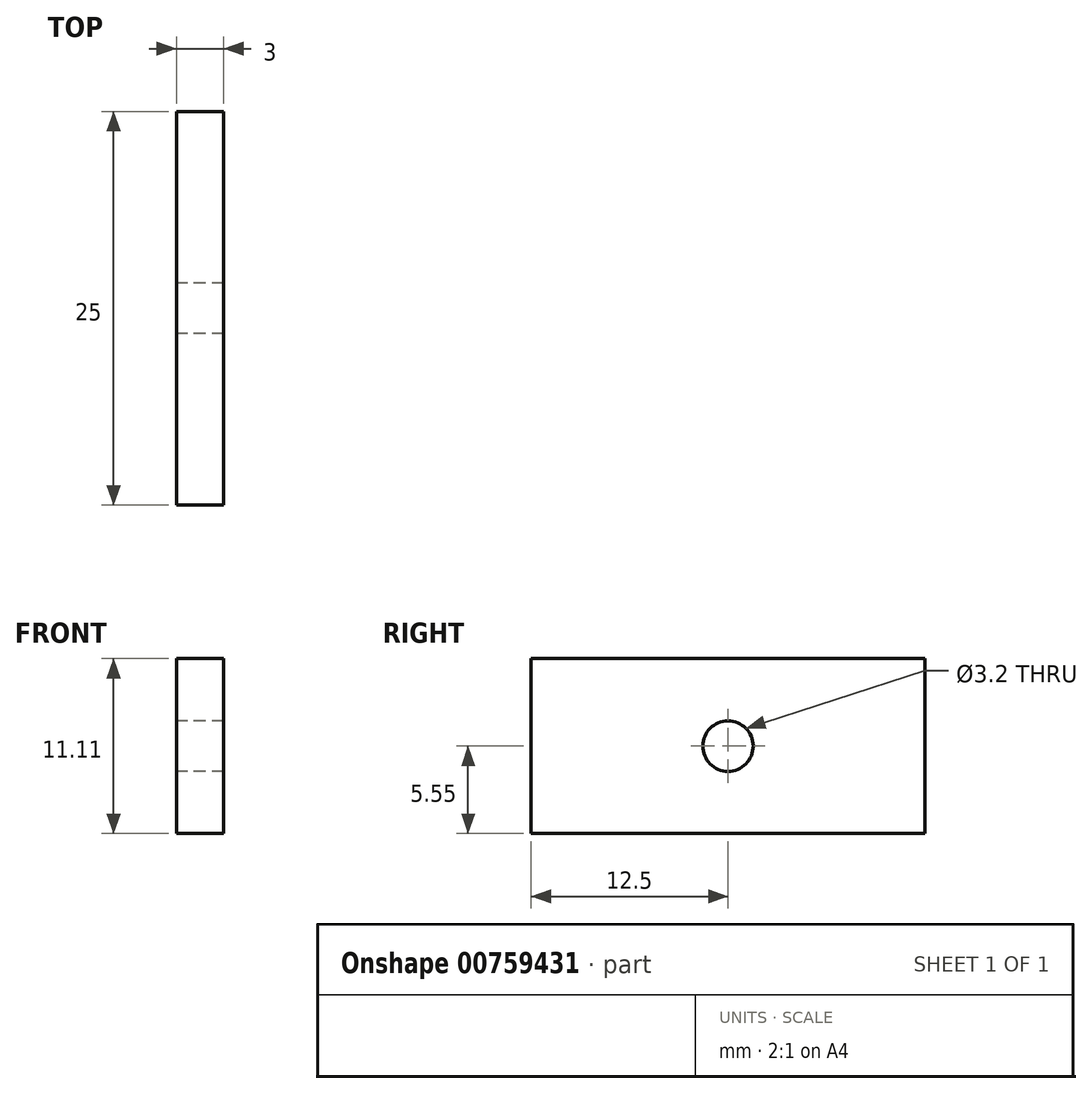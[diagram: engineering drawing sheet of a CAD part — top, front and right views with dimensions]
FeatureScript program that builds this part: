
annotation { "Feature Type Name" : "Feature", "Feature Type Description" : "" }
export const myFeature = defineFeature(function(context is Context, id is Id, definition is map)
    precondition{}
    {
        {
            var Q0;
            Q0=qCreatedBy(makeId("Right.planeOp"),FACE);
            var sketch = newSketch(context, id + "F0", { "sketchPlane" : qUnion([Q0])});
            skLineSegment(sketch, "E0.bottom", {"start": v(12.5, 5.56) * mm, "end": v(-12.5, 5.56) * mm});
            skLineSegment(sketch, "E0.top", {"start": v(12.5, -5.55) * mm, "end": v(-12.5, -5.55) * mm});
            skLineSegment(sketch, "E0.left", {"start": v(12.5, 5.56) * mm, "end": v(12.5, -5.55) * mm});
            skLineSegment(sketch, "E0.right", {"start": v(-12.5, 5.56) * mm, "end": v(-12.5, -5.55) * mm});
            skPoint(sketch, "E0.middle", {"position": v(0, 0) * mm});
            skCircle(sketch, "E1", {"center": v(0, 0) * mm, "radius": 1.6 * mm});
            skSolve(sketch);
        }
        {
            var Q0;
            Q0 = qSketchRegion(id + "F0", true);
            extrude(context, id + "F1", {"entities" : qUnion([Q0]), "endBound" : BoundingType.SYMMETRIC, "depth" : 3 * mm, "offsetDistance" : 25 * mm});
        }
    });
